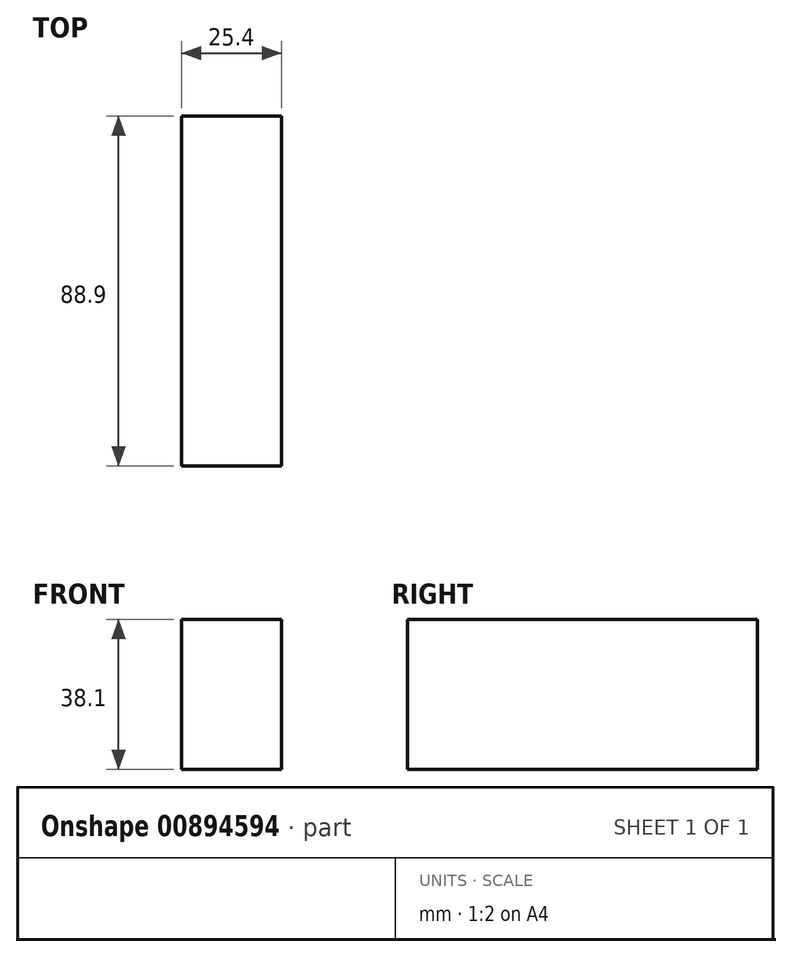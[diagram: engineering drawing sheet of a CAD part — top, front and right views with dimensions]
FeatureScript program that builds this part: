
annotation { "Feature Type Name" : "Feature", "Feature Type Description" : "" }
export const myFeature = defineFeature(function(context is Context, id is Id, definition is map)
    precondition{}
    {
        {
            var Q0;
            Q0=qCreatedBy(makeId("Right.planeOp"),FACE);
            var sketch = newSketch(context, id + "F0", { "sketchPlane" : qUnion([Q0])});
            skLineSegment(sketch, "E0.bottom", {"start": v(-44.45, 0) * mm, "end": v(44.45, 0) * mm});
            skLineSegment(sketch, "E0.top", {"start": v(-44.45, 38.1) * mm, "end": v(44.45, 38.1) * mm});
            skLineSegment(sketch, "E0.left", {"start": v(-44.45, 0) * mm, "end": v(-44.45, 38.1) * mm});
            skLineSegment(sketch, "E0.right", {"start": v(44.45, 0) * mm, "end": v(44.45, 38.1) * mm});
            skSolve(sketch);
        }
        {
            var Q0;
            Q0=makeQuery(id+"F0.imprint","IMPRINT",FACE,{"disambiguationData":[TD([[makeQuery(id+"F0.imprint","IMPRINT",EDGE,{"derivedFrom":sQuery(id+"F0.wireOp",EDGE,"E0.bottom")}),1.0]])]});
            extrude(context, id + "F1", {"entities" : qUnion([Q0]), "endBound" : BoundingType.SYMMETRIC, "depth" : 25.4 * mm, "offsetDistance" : 25.4 * mm});
        }
    });
